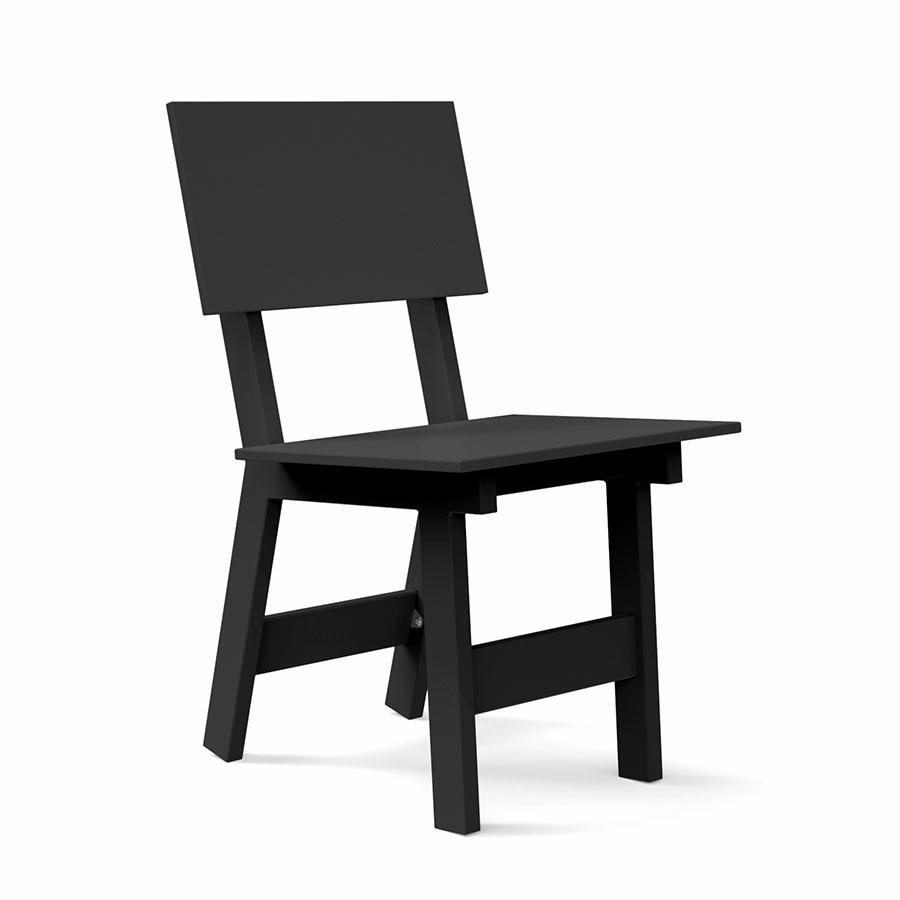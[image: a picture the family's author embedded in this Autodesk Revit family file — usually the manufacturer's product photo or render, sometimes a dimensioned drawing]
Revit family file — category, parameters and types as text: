
# Revit family: Lollygagger Salmela Gladys
name_source: partatom
category: Furniture
revit_build: Autodesk Revit 2016 (Build: 20150220_1215(x64)
units: mm (PartAtom-declared; Revit-internal decimal feet)

## family parameters
Always vertical = Yes
Cut with Voids When Loaded = No
OmniClass Number = 23.40.20.00
OmniClass Title = General Furniture and Specialties
Room Calculation Point = No
Shared = No
Work Plane-Based = No

## types (10) — shared parameters
Height = 43"
Length = 20"
Manufacturer = Loll
Thick = 5/8"
Type Image = Salmela Emin HD.jpg
URL = https://lolldesigns.com
Width = 31 5/32"

## per-type parameters (varying)
| type | Finish Material |
| Loll-Black | Loll-Driftwood |
| Loll-Sunset | Loll-Sunset |
| Loll-Chocolate | Loll-Chocolate |
| Loll-Sky | Loll-Sky |
| Loll-Apple | Loll-Apple |
| Loll-Leaf | Loll-Leaf |
| Loll-Charcoal | Loll-Charcoal |
| Loll-Navy Blue | Loll-Navy Blue |
| Loll-White | Loll-White |
| Loll-Driftwood | Loll-Driftwood |

## geometry (parser evidence)
native form markers: Sweep x3
no freeform markers — native parametric forms only
